# Revit family: IS_ConnectAir_E1148_BIM_DE
name_source: partatom
category: Plumbing Fixtures
revit_build: Autodesk Revit MEP 2016 (Build: 20161004_0715(x64)
units: mm (PartAtom-declared; Revit-internal decimal feet)

## family parameters
Always vertical = No
Cut with Voids When Loaded = No
OmniClass Number = 23.45.05.14.21.11
OmniClass Title = Bath/Shower Units
Part Type = Normal
Room Calculation Point = No
Round Connector Dimension = Use Diameter
Shared = No
Work Plane-Based = No

## types (1)
- E114801 - CONNECT AIR sidepanel for shower bath tub 700x560mm
    Accessories = www.idealstandard.de\ersatzteile
    AssetType = Fixed
    BIMObjectName = ISI_IdealStandard_Baths_ConnectAir_E114801
    BIMobject category = Screens & Dividers
    BOSUseNativeGeometries = 1
    BarCode = 5017830520993
    Brand = Ideal Standard
    Brand url = http://www.idealstandard.de
    Color = White
    ConnectionType = Plumbing
    Cost = 0 $
    CurrencyUnit = €
    CurrentRevision = 1
    Date of publishing = 20/12/2017
    Description = IS Seitenschürze CONNECT AIR f. Dusch-BW Version re.o.li., 700x510mm, Weiß
    DrainSize = 0 mm  [stored 0 ft]
    DurationUnit = Year
    EAN code = https://5017830520993
    Edition number = 1
    ExpectedLife = 25
    Features = IS Seitenschürze CONNECT AIR f. Dusch-BW Version re.o.li., 700x510mm, Weiß
    Finish = White
    IFC Classification = Sanitary Terminal
    IfcExportAs = IfcSanitaryTerminalType
    Installation instructions = http://www.idealstandard.de
    InstallationInstructions = www.idealstandard.de\produkte
    MainColor = White
    MaintenanceInformation = www.idealstandard.de\produkte
    Manufacturer name = Ideal Standard
    ManufacturerURL = http://www.idealstandard.de
    Material = Sanitary Brass
    Material main = Acrylic
    MaterialThickness = 0 mm  [stored 0 ft]
    Model = E114801
    ModelNumber = E114801
    ModelReference = IS Seitenschürze CONNECT AIR f. Dusch-BW Version re.o.li., 700x510mm, Weiß
    NBS Reference Code = 35-06-08
    NBS Reference Description = Baths
    Name = Baths_ConnectAir_E114801
    NettWeight = 1.3 Kg
    Nominal height = 560
    Nominal width = 700
    NominalDepth = 16 mm  [stored 0.0524934 ft]
    NominalHeight = 524 mm  [stored 1.71916 ft]
    NominalLength = 16 mm  [stored 0.0524934 ft]
    NominalWidth = 688 mm
    OmniClass Code = 23-31 15 00
    OmniClass Description = Bathtubs
    Product Guid = bc2a7590-5252-41b8-a918-62e958f063d0
    Product SKU = E1148
    Product data url = https://bimobject.com
    Product family = Sanitary
    Product group = Bath Panel
    Product name = CONNECT AIR sidepanel for shower bath tub 700x560mm
    Product url = http://www.idealstandard.de
    ProductInformation = www.idealstandard.de/produkte
    QR code = http://bimobject.com
    Shape = Rectangular
    Size = 524 x 16 x 688mm
    Space = Internal
    SpareParts = www.idealstandard.de/ersatzteile
    Technical description = http://www.idealstandard.de
    URL = http://www.idealstandard.de
    Uniclass 1.4 Code = L7211
    Uniclass 1.4 Description = Baths
    Uniclass 2.0 Code = PR-35-06-08
    Uniclass 2.0 Description = Baths
    Uniclass 2015 Code = Pr_40_20_06_08
    Uniclass 2015 Name = Baths
    Uniclass2015Code = Pr_40_20_06_08
    Uniclass2015Title = Baths
    Uniclass2015Version = Products v1.1
    Version = 1
    VolumeUnits = Litres
    Weight Net (Kg) = 1.3

note: [stored X ft] marks values corroborated as IEEE doubles in the binary element streams (Revit-internal decimal feet)

## geometry (parser evidence)
native form markers: Blend x4, Sweep x1
no freeform markers — native parametric forms only
